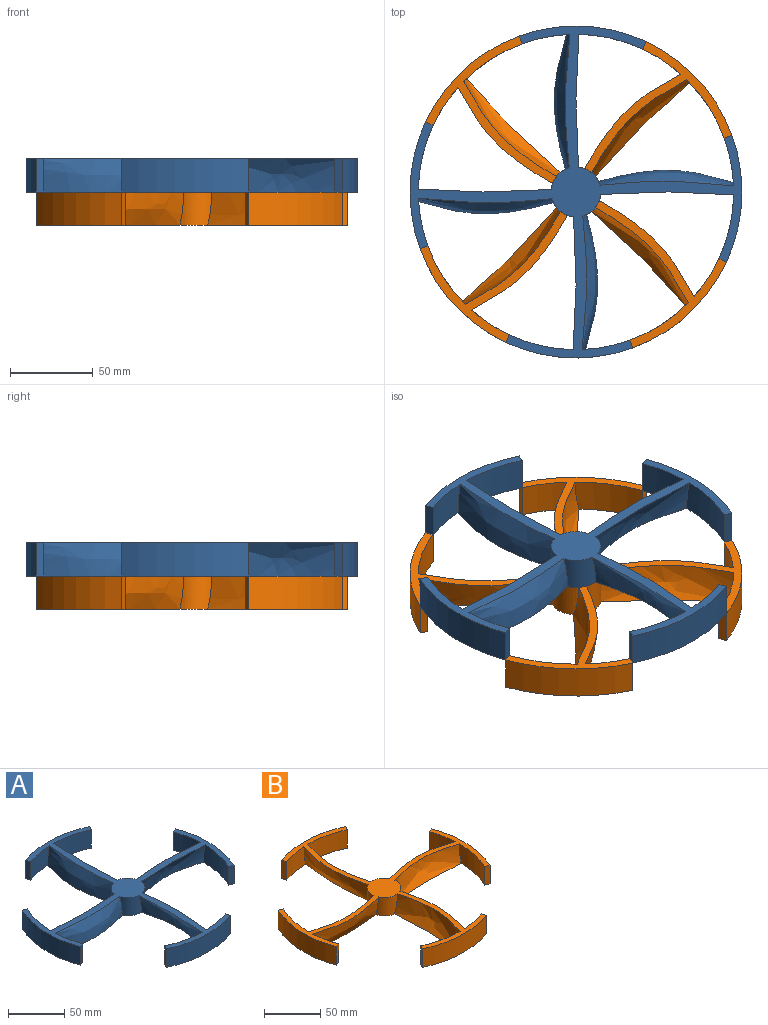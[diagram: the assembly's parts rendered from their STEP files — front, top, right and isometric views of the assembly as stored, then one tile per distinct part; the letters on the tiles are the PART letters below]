
ASSEMBLY  parts=2 mates=1
PART A: 34 faces, bbox 200.4x200.4x20.4 mm
  f0: cylinder r=15mm len=20mm, axis (0,0,-1), area 366.7mm2, adj f3,f4,f6,f14
  f1: cylinder r=15mm len=20mm, axis (0,0,-1), area 366.7mm2, adj f3,f4,f7,f21
  f2: cylinder r=15mm len=20mm, axis (0,0,-1), area 366.7mm2, adj f3,f4,f13,f23
  f3: plane 200.42x200.42mm, normal (0,0,1), area 4211.3mm2, adj f0,f1,f2,f5,f6,f7,f8,f9
  f4: plane 200.29x200.29mm, normal (0,0,-1), area 3850.5mm2, adj f0,f1,f2,f5,f6,f7,f8,f9
  f5: cylinder r=15mm len=20mm, axis (0,0,-1), area 366.7mm2, adj f3,f4,f20,f22
  f6: bspline ~81.35x20mm, area 1709.6mm2, adj f0,f3,f4,f29
  f7: bspline ~80.1x20mm, area 1727.7mm2, adj f1,f3,f4,f30
  f8: cylinder r=95mm len=28.78mm, axis (0,0,-1), area 568.9mm2, adj f3,f4,f9,f13
  f9: plane 20x4.7mm, normal (-0.34,0.94,0), area 100mm2, adj f3,f4,f8,f10
  f10: cylinder r=100mm len=76.46mm, axis (0,0,-1), area 1570.8mm2, adj f3,f4,f9,f11
  f11: plane 20x4.53mm, normal (-0.42,-0.91,0), area 100mm2, adj f3,f4,f10,f12
  f12: cylinder r=95mm len=40.82mm, axis (0,0,-1), area 818.3mm2, adj f3,f4,f11,f14
  f13: bspline ~81.35x20mm, area 1709.6mm2, adj f2,f3,f4,f8
  f14: bspline ~80.1x20mm, area 1727.7mm2, adj f0,f3,f4,f12
  f15: cylinder r=95mm len=28.78mm, axis (0,0,-1), area 568.9mm2, adj f3,f4,f16,f21
  f16: plane 20x4.7mm, normal (0.34,-0.94,0), area 100mm2, adj f3,f4,f15,f17
  f17: cylinder r=100mm len=76.46mm, axis (0,0,-1), area 1570.8mm2, adj f3,f4,f16,f18
  f18: plane 20x4.53mm, normal (0.42,0.91,0), area 100mm2, adj f3,f4,f17,f19
  f19: cylinder r=95mm len=40.82mm, axis (0,0,-1), area 818.3mm2, adj f3,f4,f18,f20
  f20: bspline ~80.1x20mm, area 1727.7mm2, adj f3,f4,f5,f19
  f21: bspline ~81.35x20mm, area 1709.6mm2, adj f1,f3,f4,f15
  f22: bspline ~81.35x20mm, area 1709.6mm2, adj f3,f4,f5,f24
  f23: bspline ~80.1x20mm, area 1727.7mm2, adj f2,f3,f4,f28
  f24: cylinder r=95mm len=28.78mm, axis (0,0,-1), area 568.9mm2, adj f3,f4,f22,f27
  f25: plane 20x4.53mm, normal (0.91,-0.42,0), area 100mm2, adj f3,f4,f26,f28
  f26: cylinder r=100mm len=76.46mm, axis (0,0,-1), area 1570.8mm2, adj f3,f4,f25,f27
  f27: plane 20x4.7mm, normal (-0.94,-0.34,0), area 100mm2, adj f3,f4,f24,f26
  f28: cylinder r=95mm len=40.82mm, axis (0,0,-1), area 818.3mm2, adj f3,f4,f23,f25
  f29: cylinder r=95mm len=28.78mm, axis (0,0,-1), area 568.9mm2, adj f3,f4,f6,f33
  f30: cylinder r=95mm len=40.82mm, axis (0,0,-1), area 818.3mm2, adj f3,f4,f7,f31
  f31: plane 20x4.53mm, normal (-0.91,0.42,0), area 100mm2, adj f3,f4,f30,f32
  f32: cylinder r=100mm len=76.46mm, axis (0,0,-1), area 1570.8mm2, adj f3,f4,f31,f33
  f33: plane 20x4.7mm, normal (0.94,0.34,0), area 100mm2, adj f3,f4,f29,f32
PART B: 34 faces, bbox 200.4x200.4x20.4 mm
  f0: cylinder r=15mm len=20mm, axis (0,0,-1), area 366.7mm2, adj f24,f25,f28,f33
  f1: cylinder r=15mm len=20mm, axis (0,0,-1), area 366.7mm2, adj f24,f26,f30,f33
  f2: cylinder r=15mm len=20mm, axis (0,0,-1), area 366.7mm2, adj f24,f27,f32,f33
  f3: cylinder r=15mm len=20mm, axis (0,0,-1), area 366.7mm2, adj f24,f29,f31,f33
  f4: cylinder r=95mm len=28.78mm, axis (0,0,-1), area 568.9mm2, adj f5,f24,f27,f33
  f5: plane 20x4.7mm, normal (-0.34,0.94,0), area 100mm2, adj f4,f6,f24,f33
  f6: cylinder r=100mm len=76.46mm, axis (0,0,-1), area 1570.8mm2, adj f5,f7,f24,f33
  f7: plane 20x4.53mm, normal (-0.42,-0.91,0), area 100mm2, adj f6,f8,f24,f33
  f8: cylinder r=95mm len=40.82mm, axis (0,0,-1), area 818.3mm2, adj f7,f24,f28,f33
  f9: cylinder r=95mm len=28.78mm, axis (0,0,-1), area 568.9mm2, adj f10,f24,f30,f33
  f10: plane 20x4.7mm, normal (0.34,-0.94,0), area 100mm2, adj f9,f11,f24,f33
  f11: cylinder r=100mm len=76.46mm, axis (0,0,-1), area 1570.8mm2, adj f10,f12,f24,f33
  f12: plane 20x4.53mm, normal (0.42,0.91,0), area 100mm2, adj f11,f13,f24,f33
  f13: cylinder r=95mm len=40.82mm, axis (0,0,-1), area 818.3mm2, adj f12,f24,f29,f33
  f14: cylinder r=95mm len=28.78mm, axis (0,0,-1), area 568.9mm2, adj f17,f24,f31,f33
  f15: plane 20x4.53mm, normal (0.91,-0.42,0), area 100mm2, adj f16,f18,f24,f33
  f16: cylinder r=100mm len=76.46mm, axis (0,0,-1), area 1570.8mm2, adj f15,f17,f24,f33
  f17: plane 20x4.7mm, normal (-0.94,-0.34,0), area 100mm2, adj f14,f16,f24,f33
  f18: cylinder r=95mm len=40.82mm, axis (0,0,-1), area 818.3mm2, adj f15,f24,f32,f33
  f19: cylinder r=95mm len=28.78mm, axis (0,0,-1), area 568.9mm2, adj f23,f24,f25,f33
  f20: cylinder r=95mm len=40.82mm, axis (0,0,-1), area 818.3mm2, adj f21,f24,f26,f33
  f21: plane 20x4.53mm, normal (-0.91,0.42,0), area 100mm2, adj f20,f22,f24,f33
  f22: cylinder r=100mm len=76.46mm, axis (0,0,-1), area 1570.8mm2, adj f21,f23,f24,f33
  f23: plane 20x4.7mm, normal (0.94,0.34,0), area 100mm2, adj f19,f22,f24,f33
  f24: plane 200.42x200.42mm, normal (0,0,-1), area 4211.3mm2, adj f0,f1,f2,f3,f4,f5,f6,f7
  f25: bspline ~81.35x20mm, area 1709.6mm2, adj f0,f19,f24,f33
  f26: bspline ~80.1x20mm, area 1727.7mm2, adj f1,f20,f24,f33
  f27: bspline ~81.35x20mm, area 1709.6mm2, adj f2,f4,f24,f33
  f28: bspline ~80.1x20mm, area 1727.7mm2, adj f0,f8,f24,f33
  f29: bspline ~80.1x20mm, area 1727.7mm2, adj f3,f13,f24,f33
  f30: bspline ~81.35x20mm, area 1709.6mm2, adj f1,f9,f24,f33
  f31: bspline ~81.35x20mm, area 1709.6mm2, adj f3,f14,f24,f33
  f32: bspline ~80.1x20mm, area 1727.7mm2, adj f2,f18,f24,f33
  f33: plane 200.3x200.3mm, normal (0,0,1), area 3845.6mm2, adj f0,f1,f2,f3,f4,f5,f6,f7
PLACE A t=(53.55,124.51,-13.72)mm
PLACE B rot(axis=(0,0,-1),45deg) t=(53.55,124.51,-13.72)mm
MATE fastened A.f11 <-> B.f5  axis (-0.42,-0.91,0) through (141.91,83.3,-13.72)mm
